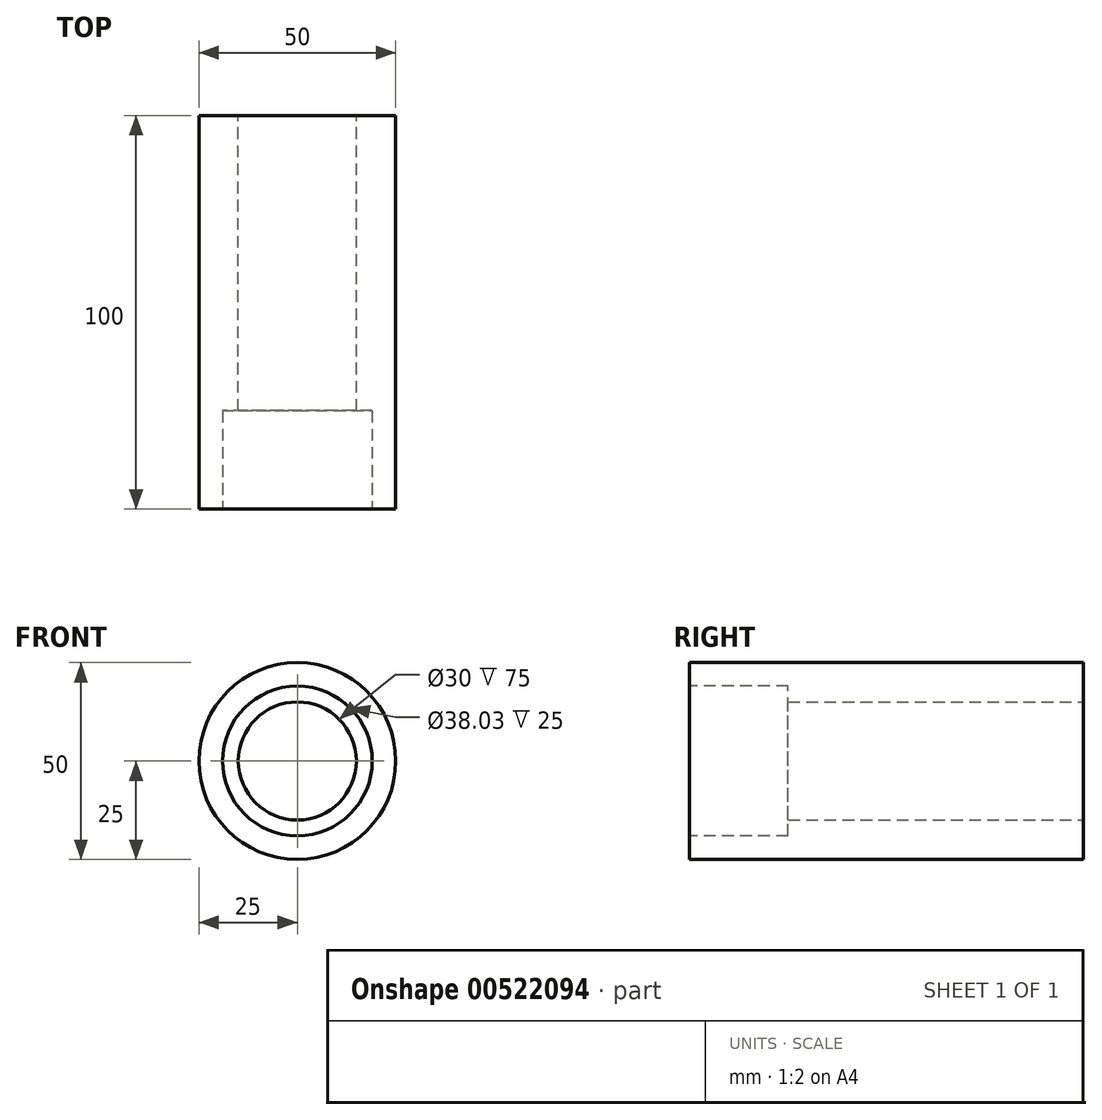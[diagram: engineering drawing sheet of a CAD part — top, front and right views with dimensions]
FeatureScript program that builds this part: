
annotation { "Feature Type Name" : "Feature", "Feature Type Description" : "" }
export const myFeature = defineFeature(function(context is Context, id is Id, definition is map)
    precondition{}
    {
        {
            var Q0;
            Q0=qCreatedBy(makeId("Front.planeOp"),FACE);
            var sketch = newSketch(context, id + "F0", { "sketchPlane" : qUnion([Q0])});
            skCircle(sketch, "E0", {"center": v(0, 0) * mm, "radius": 25 * mm});
            skCircle(sketch, "E1", {"center": v(0, 0) * mm, "radius": 15 * mm});
            skSolve(sketch);
        }
        {
            var Q0;
            Q0 = qSketchRegion(id + "F0", true);
            extrude(context, id + "F1", {"entities" : qUnion([Q0]), "depth" : 100 * mm, "offsetDistance" : 25 * mm});
        }
        {
            var Q0;
            Q0=makeQuery(id+"F1.opExtrude","CAP_FACE",FACE,{"disambiguationData":[OSD([sQuery(id+"F0.wireOp",EDGE,"E0"),sQuery(id+"F0.wireOp",EDGE,"E1")])],"isStart":false});
            var sketch = newSketch(context, id + "F2", { "sketchPlane" : qUnion([Q0])});
            skCircle(sketch, "E2", {"center": v(0, 0) * mm, "radius": 19.01 * mm});
            skSolve(sketch);
        }
        {
            var Q0;
            Q0 = qSketchRegion(id + "F2", true);
            extrude(context, id + "F3", {"entities" : qUnion([Q0]), "operationType" : NewBodyOperationType.REMOVE, "oppositeDirection" : true, "depth" : 25 * mm, "offsetDistance" : 25 * mm});
        }
    });
